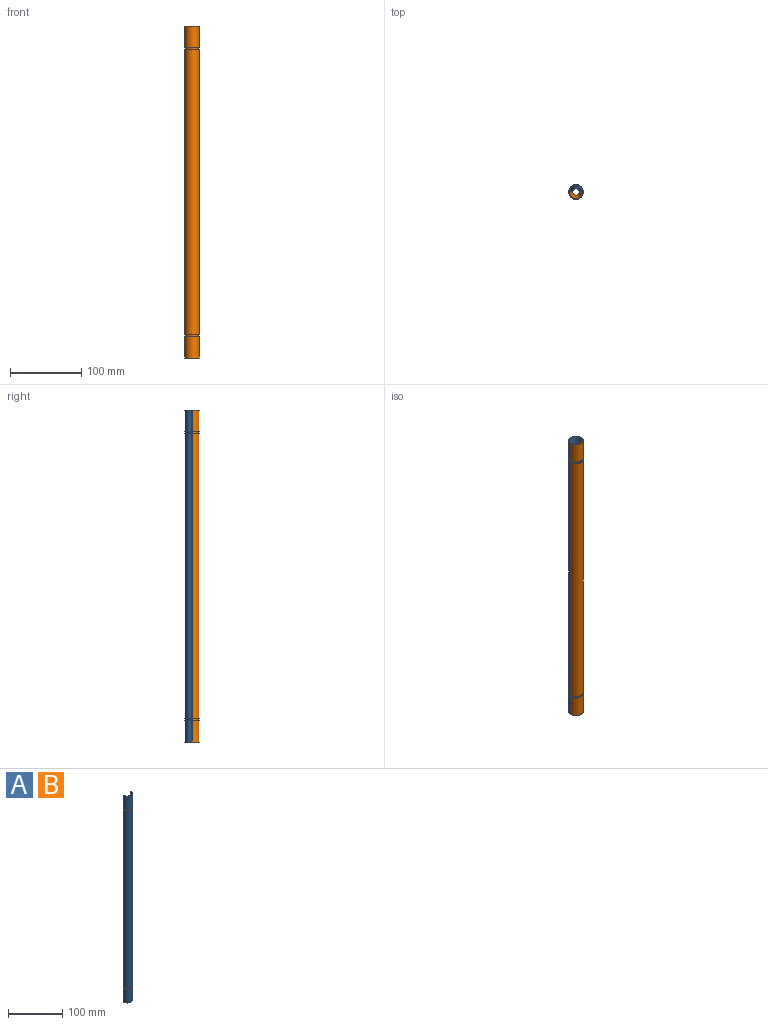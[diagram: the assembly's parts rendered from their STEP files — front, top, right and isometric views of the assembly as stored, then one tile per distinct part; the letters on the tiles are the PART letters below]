
ASSEMBLY  parts=2 mates=1
PART A: 22 faces, bbox 20x10x466 mm
  f0: plane 466x4.49mm, normal (0,1,0), area 1974.7mm2, adj f3,f4,f5,f6,f8,f9,f11,f13
  f1: plane 466x4.49mm, normal (0,1,0), area 1974.7mm2, adj f3,f4,f5,f6,f7,f9,f11,f13
  f2: cylinder r=10mm len=30mm, axis (0,0,-1), area 910.9mm2, adj f3,f4,f7,f8
  f3: plane 19.97x10mm, normal (0,0,1), area 17.9mm2, adj f0,f1,f2,f6,f7,f8
  f4: plane 19.97x10mm, normal (0,0,-1), area 43.5mm2, adj f0,f1,f2,f7,f8,f9
  f5: cylinder r=5mm len=416mm, axis (0,0,1), area 6534.5mm2, adj f0,f1,f6,f15
  f6: cone r=5mm half-angle=10deg, axis (0,0,1), area 574.5mm2, adj f0,f1,f3,f5
  f7: cylinder r=0.5mm len=30mm, axis (0,0,-1), area 24.4mm2, adj f1,f2,f3,f4
  f8: cylinder r=0.5mm len=30mm, axis (0,0,-1), area 24.4mm2, adj f0,f2,f3,f4
  f9: cylinder r=8.5mm len=17mm, axis (0,0,1), area 80.1mm2, adj f0,f1,f4,f11
  f10: cylinder r=10mm len=400mm, axis (0,0,1), area 12145.1mm2, adj f11,f19,f20,f21
  f11: plane 19.97x10mm, normal (0,0,1), area 43.5mm2, adj f0,f1,f9,f10,f20,f21
  f12: cylinder r=10mm len=30mm, axis (0,0,1), area 910.9mm2, adj f13,f14,f16,f17
  f13: plane 19.97x10mm, normal (0,0,-1), area 17.9mm2, adj f0,f1,f12,f15,f16,f17
  f14: plane 19.97x10mm, normal (0,0,1), area 43.5mm2, adj f0,f1,f12,f16,f17,f18
  f15: cone r=5mm half-angle=10deg, axis (0,0,-1), area 574.5mm2, adj f0,f1,f5,f13
  f16: cylinder r=0.5mm len=30mm, axis (0,0,1), area 24.4mm2, adj f1,f12,f13,f14
  f17: cylinder r=0.5mm len=30mm, axis (0,0,1), area 24.4mm2, adj f0,f12,f13,f14
  f18: cylinder r=8.5mm len=17mm, axis (0,0,-1), area 80.1mm2, adj f0,f1,f14,f19
  f19: plane 19.97x10mm, normal (0,0,-1), area 43.5mm2, adj f0,f1,f10,f18,f20,f21
  f20: cylinder r=0.5mm len=400mm, axis (0,0,1), area 324.7mm2, adj f0,f10,f11,f19
  f21: cylinder r=0.5mm len=400mm, axis (0,0,1), area 324.7mm2, adj f1,f10,f11,f19
PART B: same geometry as A
PLACE A rot(axis=(0,0,1),180deg) t=(0.04,0.82,41.84)mm
PLACE B t=(0.09,0.75,41.84)mm
MATE parallel A.f1 <-> B.f1  axis (0,-1,0) through (7.33,0.82,-176.16)mm
